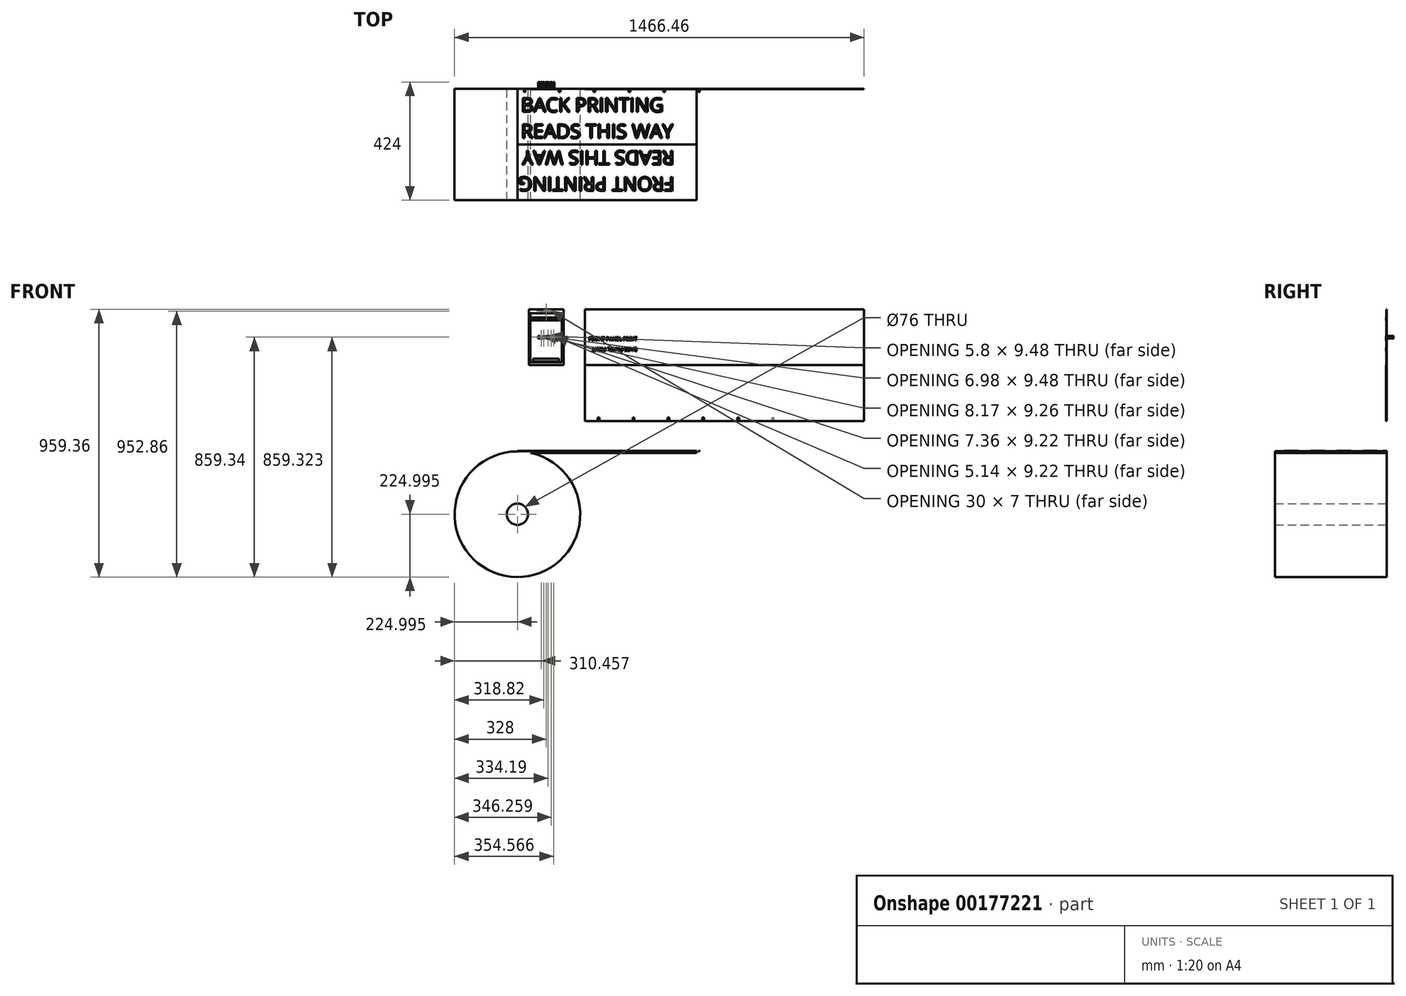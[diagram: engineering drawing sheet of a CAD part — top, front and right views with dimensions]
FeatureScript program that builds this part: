
annotation { "Feature Type Name" : "Feature", "Feature Type Description" : "" }
export const myFeature = defineFeature(function(context is Context, id is Id, definition is map)
    precondition{}
    {
        {
            assignVariable(context, id + "F0", {"name" : "hoogte", "anyValue" : 200});
        }
        {
            var Q0;
            Q0=qCreatedBy(makeId("Front.planeOp"),FACE);
            var sketch = newSketch(context, id + "F1", { "sketchPlane" : qUnion([Q0])});
            skLineSegment(sketch, "E0.bottom", {"start": v(-62.5, 100) * mm, "end": v(62.5, 100) * mm});
            skLineSegment(sketch, "E0.top", {"start": v(-62.5, -100) * mm, "end": v(62.5, -100) * mm});
            skLineSegment(sketch, "E0.left", {"start": v(-62.5, 100) * mm, "end": v(-62.5, -100) * mm});
            skLineSegment(sketch, "E0.right", {"start": v(62.5, 100) * mm, "end": v(62.5, -100) * mm});
            skLineSegment(sketch, "E1", {"start": v(-62.5, 76.41) * mm, "end": v(-61.09, 75) * mm});
            skLineSegment(sketch, "E2", {"start": v(-61.09, 75) * mm, "end": v(-62.5, 73.59) * mm});
            skLineSegment(sketch, "E3", {"start": v(62.5, 76.41) * mm, "end": v(61.09, 75) * mm});
            skLineSegment(sketch, "E4", {"start": v(61.09, 75) * mm, "end": v(62.5, 73.59) * mm});
            skLineSegment(sketch, "E5.bottom", {"start": v(138.46, 100) * mm, "end": v(1138.46, 100) * mm});
            skLineSegment(sketch, "E5.top", {"start": v(138.46, -300) * mm, "end": v(1138.46, -300) * mm});
            skLineSegment(sketch, "E5.left", {"start": v(138.46, 100) * mm, "end": v(138.46, -300) * mm});
            skLineSegment(sketch, "E5.right", {"start": v(1138.46, 100) * mm, "end": v(1138.46, -300) * mm});
            skLineSegment(sketch, "E6", {"start": v(138.46, -100) * mm, "end": v(1138.46, -100) * mm});
            skLineSegment(sketch, "E7", {"start": v(-62.5, 100) * mm, "end": v(62.5, -100) * mm, "construction": true});
            skLineSegment(sketch, "E8", {"start": v(62.5, 100) * mm, "end": v(-62.5, -100) * mm, "construction": true});
            skPoint(sketch, "E9", {"position": v(0, 0) * mm});
            skSolve(sketch);
        }
        {
            var Q0;
            {var subQ3=sQuery(id+"F1.wireOp",EDGE,"E0.bottom");Q0=makeQuery(id+"F1.imprint","IMPRINT",FACE,{"disambiguationData":[TD([[makeQuery(id+"F1.imprint","IMPRINT",EDGE,{"derivedFrom":subQ3}),-1.0]])]});}
            var Q1;
            Q1=makeQuery(id+"F1.imprint","IMPRINT",FACE,{"disambiguationData":[TD([[makeQuery(id+"F1.imprint","IMPRINT",EDGE,{"derivedFrom":sQuery(id+"F1.wireOp",EDGE,"E5.bottom")}),-1.0]])]});
            var Q2;
            {var subQ0=sQuery(id+"F1.wireOp",EDGE,"E5.top");Q2=makeQuery(id+"F1.imprint","IMPRINT",FACE,{"disambiguationData":[TD([[makeQuery(id+"F1.imprint","IMPRINT",EDGE,{"derivedFrom":subQ0}),1.0]])]});}
            extrude(context, id + "F2", {"entities" : qUnion([Q0, Q1, Q2]), "depth" : 1 * mm});
        }
        {
            var Q0;
            Q0=makeQuery(id+"F2.opExtrude","CAP_FACE",FACE,{"disambiguationData":[OSD([sQuery(id+"F1.wireOp",EDGE,"E0.bottom"),sQuery(id+"F1.wireOp",EDGE,"E0.top"),sQuery(id+"F1.wireOp",EDGE,"E0.left"),sQuery(id+"F1.wireOp",EDGE,"E0.right"),sQuery(id+"F1.wireOp",EDGE,"E1"),sQuery(id+"F1.wireOp",EDGE,"E2"),sQuery(id+"F1.wireOp",EDGE,"E3"),sQuery(id+"F1.wireOp",EDGE,"E4")])],"isStart":false});
            var sketch = newSketch(context, id + "F3", { "sketchPlane" : qUnion([Q0])});
            skLineSegment(sketch, "E10.0.0", {"start": v(62.5, 100) * mm, "end": v(-62.5, 100) * mm});
            skLineSegment(sketch, "E10.0.1", {"start": v(-62.5, 100) * mm, "end": v(-62.5, 76.41) * mm});
            skLineSegment(sketch, "E10.0.2", {"start": v(-62.5, 76.41) * mm, "end": v(-61.09, 75) * mm});
            skLineSegment(sketch, "E10.0.3", {"start": v(-61.09, 75) * mm, "end": v(-62.5, 73.59) * mm});
            skLineSegment(sketch, "E10.0.4", {"start": v(-62.5, 73.59) * mm, "end": v(-62.5, -100) * mm});
            skLineSegment(sketch, "E10.0.5", {"start": v(-62.5, -100) * mm, "end": v(62.5, -100) * mm});
            skLineSegment(sketch, "E10.0.6", {"start": v(62.5, -100) * mm, "end": v(62.5, 73.59) * mm});
            skLineSegment(sketch, "E10.0.7", {"start": v(62.5, 73.59) * mm, "end": v(61.09, 75) * mm});
            skLineSegment(sketch, "E10.0.8", {"start": v(61.09, 75) * mm, "end": v(62.5, 76.41) * mm});
            skLineSegment(sketch, "E10.0.9", {"start": v(62.5, 76.41) * mm, "end": v(62.5, 100) * mm});
            skLineSegment(sketch, "E11.bottom", {"start": v(-56.5, 85) * mm, "end": v(56.5, 85) * mm});
            skLineSegment(sketch, "E11.top", {"start": v(-56.5, -90) * mm, "end": v(56.5, -90) * mm});
            skLineSegment(sketch, "E11.left", {"start": v(-56.5, 85) * mm, "end": v(-56.5, -90) * mm});
            skLineSegment(sketch, "E11.right", {"start": v(56.5, 85) * mm, "end": v(56.5, -90) * mm});
            skLineSegment(sketch, "E12.bottom", {"start": v(-62.5, 100) * mm, "end": v(-59.5, 100) * mm});
            skLineSegment(sketch, "E12.top", {"start": v(-62.5, 88) * mm, "end": v(-59.5, 88) * mm});
            skLineSegment(sketch, "E12.left", {"start": v(-62.5, 100) * mm, "end": v(-62.5, 88) * mm});
            skLineSegment(sketch, "E12.right", {"start": v(-59.5, 100) * mm, "end": v(-59.5, 88) * mm});
            skLineSegment(sketch, "E13.bottom", {"start": v(62.5, 100) * mm, "end": v(59.5, 100) * mm});
            skLineSegment(sketch, "E13.top", {"start": v(62.5, 88) * mm, "end": v(59.5, 88) * mm});
            skLineSegment(sketch, "E13.left", {"start": v(62.5, 100) * mm, "end": v(62.5, 88) * mm});
            skLineSegment(sketch, "E13.right", {"start": v(59.5, 100) * mm, "end": v(59.5, 88) * mm});
            skLineSegment(sketch, "E14.bottom", {"start": v(-46.5, -77) * mm, "end": v(46.5, -77) * mm});
            skLineSegment(sketch, "E14.top", {"start": v(-46.5, -87) * mm, "end": v(46.5, -87) * mm});
            skLineSegment(sketch, "E14.left", {"start": v(-46.5, -77) * mm, "end": v(-46.5, -87) * mm});
            skLineSegment(sketch, "E14.right", {"start": v(46.5, -77) * mm, "end": v(46.5, -87) * mm});
            skSolve(sketch);
        }
        {
            var Q0;
            Q0=makeQuery(id+"F3.imprint","IMPRINT",FACE,{"disambiguationData":[TD([[makeQuery(id+"F3.imprint","IMPRINT",EDGE,{"derivedFrom":sQuery(id+"F3.wireOp",EDGE,"E11.bottom")}),-1.0]])]});
            var Q1;
            Q1=makeQuery(id+"F3.imprint","IMPRINT",FACE,{"disambiguationData":[TD([[makeQuery(id+"F3.imprint","IMPRINT",EDGE,{"derivedFrom":sQuery(id+"F3.wireOp",EDGE,"E12.bottom")}),-1.0]])]});
            var Q2;
            Q2=makeQuery(id+"F3.imprint","IMPRINT",FACE,{"disambiguationData":[TD([[makeQuery(id+"F3.imprint","IMPRINT",EDGE,{"derivedFrom":sQuery(id+"F3.wireOp",EDGE,"E13.bottom")}),-1.0]])]});
            extrude(context, id + "F4", {"entities" : qUnion([Q0, Q1, Q2]), "operationType" : NewBodyOperationType.REMOVE, "oppositeDirection" : true, "depth" : 0.5 * mm});
        }
        {
            var Q0;
            Q0=makeQuery(id+"F2.opExtrude","CAP_FACE",FACE,{"disambiguationData":[OSD([sQuery(id+"F1.wireOp",EDGE,"E5.bottom"),sQuery(id+"F1.wireOp",EDGE,"E5.left"),sQuery(id+"F1.wireOp",EDGE,"E5.right"),sQuery(id+"F1.wireOp",EDGE,"E6")])],"isStart":false});
            var sketch = newSketch(context, id + "F5", { "sketchPlane" : qUnion([Q0])});
            skLineSegment(sketch, "E15.0.0", {"start": v(1138.46, 100) * mm, "end": v(138.46, 100) * mm});
            skLineSegment(sketch, "E15.0.1", {"start": v(138.46, 100) * mm, "end": v(138.46, 100) * mm});
            skLineSegment(sketch, "E15.0.2", {"start": v(138.46, 100) * mm, "end": v(1138.46, 100) * mm});
            skLineSegment(sketch, "E15.0.3", {"start": v(1138.46, 100) * mm, "end": v(1138.46, 100) * mm});
            skLineSegment(sketch, "E16.bottom", {"start": v(184.68, -300) * mm, "end": v(190.68, -300) * mm});
            skLineSegment(sketch, "E16.top", {"start": v(184.68, -288) * mm, "end": v(190.68, -288) * mm});
            skLineSegment(sketch, "E16.left", {"start": v(184.68, -300) * mm, "end": v(184.68, -288) * mm});
            skLineSegment(sketch, "E16.right", {"start": v(190.68, -300) * mm, "end": v(190.68, -288) * mm});
            skLineSegment(sketch, "E17.1.0.0", {"start": v(309.68, -288) * mm, "end": v(315.68, -288) * mm});
            skLineSegment(sketch, "E17.1.0.1", {"start": v(309.68, -300) * mm, "end": v(309.68, -288) * mm});
            skLineSegment(sketch, "E17.1.0.2", {"start": v(309.68, -300) * mm, "end": v(315.68, -300) * mm});
            skLineSegment(sketch, "E17.1.0.3", {"start": v(315.68, -300) * mm, "end": v(315.68, -288) * mm});
            skLineSegment(sketch, "E17.2.0.0", {"start": v(434.68, -288) * mm, "end": v(440.68, -288) * mm});
            skLineSegment(sketch, "E17.2.0.1", {"start": v(434.68, -300) * mm, "end": v(434.68, -288) * mm});
            skLineSegment(sketch, "E17.2.0.2", {"start": v(434.68, -300) * mm, "end": v(440.68, -300) * mm});
            skLineSegment(sketch, "E17.2.0.3", {"start": v(440.68, -300) * mm, "end": v(440.68, -288) * mm});
            skLineSegment(sketch, "E17.direction1", {"start": v(184.68, -300) * mm, "end": v(309.68, -300) * mm, "construction": true});
            skLineSegment(sketch, "E18.0.3.0", {"start": v(559.68, -288) * mm, "end": v(565.68, -288) * mm});
            skLineSegment(sketch, "E18.3.3.0", {"start": v(559.68, -300) * mm, "end": v(559.68, -288) * mm});
            skLineSegment(sketch, "E18.6.3.0", {"start": v(559.68, -300) * mm, "end": v(565.68, -300) * mm});
            skLineSegment(sketch, "E18.9.3.0", {"start": v(565.68, -300) * mm, "end": v(565.68, -288) * mm});
            skLineSegment(sketch, "E18.0.4.0", {"start": v(684.68, -288) * mm, "end": v(690.68, -288) * mm});
            skLineSegment(sketch, "E18.3.4.0", {"start": v(684.68, -300) * mm, "end": v(684.68, -288) * mm});
            skLineSegment(sketch, "E18.6.4.0", {"start": v(684.68, -300) * mm, "end": v(690.68, -300) * mm});
            skLineSegment(sketch, "E18.9.4.0", {"start": v(690.68, -300) * mm, "end": v(690.68, -288) * mm});
            skLineSegment(sketch, "E19.0.5.0", {"start": v(809.68, -288) * mm, "end": v(815.68, -288) * mm});
            skLineSegment(sketch, "E19.3.5.0", {"start": v(809.68, -300) * mm, "end": v(809.68, -288) * mm});
            skLineSegment(sketch, "E19.6.5.0", {"start": v(809.68, -300) * mm, "end": v(815.68, -300) * mm});
            skLineSegment(sketch, "E19.9.5.0", {"start": v(815.68, -300) * mm, "end": v(815.68, -288) * mm});
            skSolve(sketch);
        }
        {
            var Q0;
            Q0=makeQuery(id+"F5.imprint","IMPRINT",FACE,{"disambiguationData":[TD([[makeQuery(id+"F5.imprint","IMPRINT",EDGE,{"derivedFrom":sQuery(id+"F5.wireOp",EDGE,"JLQzprwf-iRJq-cmRX-vWmS-HmgRmsplr5sc.top")}),-1.0]])]});
            var Q1;
            Q1=makeQuery(id+"F5.imprint","IMPRINT",FACE,{"disambiguationData":[TD([[makeQuery(id+"F5.imprint","IMPRINT",EDGE,{"derivedFrom":sQuery(id+"F5.wireOp",EDGE,"E16.bottom")}),1.0]])]});
            var Q2;
            Q2=makeQuery(id+"F5.imprint","IMPRINT",FACE,{"disambiguationData":[TD([[makeQuery(id+"F5.imprint","IMPRINT",EDGE,{"derivedFrom":sQuery(id+"F5.wireOp",EDGE,"E17.1.0.0")}),-1.0]])]});
            var Q3;
            Q3=makeQuery(id+"F5.imprint","IMPRINT",FACE,{"disambiguationData":[TD([[makeQuery(id+"F5.imprint","IMPRINT",EDGE,{"derivedFrom":sQuery(id+"F5.wireOp",EDGE,"E17.2.0.0")}),-1.0]])]});
            var Q4;
            Q4=makeQuery(id+"F5.imprint","IMPRINT",FACE,{"disambiguationData":[TD([[makeQuery(id+"F5.imprint","IMPRINT",EDGE,{"derivedFrom":sQuery(id+"F5.wireOp",EDGE,"E18.0.3.0")}),-1.0]])]});
            var Q5;
            Q5=makeQuery(id+"F5.imprint","IMPRINT",FACE,{"disambiguationData":[TD([[makeQuery(id+"F5.imprint","IMPRINT",EDGE,{"derivedFrom":sQuery(id+"F5.wireOp",EDGE,"E18.0.4.0")}),-1.0]])]});
            var Q6;
            Q6=makeQuery(id+"F5.imprint","IMPRINT",FACE,{"disambiguationData":[TD([[makeQuery(id+"F5.imprint","IMPRINT",EDGE,{"derivedFrom":sQuery(id+"F5.wireOp",EDGE,"E19.0.5.0")}),-1.0]])]});
            extrude(context, id + "F6", {"entities" : qUnion([Q0, Q1, Q2, Q3, Q4, Q5, Q6]), "operationType" : NewBodyOperationType.REMOVE, "oppositeDirection" : true, "depth" : 0.5 * mm});
        }
        {
            var Q0;
            Q0=qCreatedBy(makeId("Front.planeOp"),FACE);
            var sketch = newSketch(context, id + "F7", { "sketchPlane" : qUnion([Q0])});
            skCircle(sketch, "E20", {"center": v(-103, -634.36) * mm, "radius": 225 * mm});
            skLineSegment(sketch, "E21.bottom", {"start": v(-103, -408.35) * mm, "end": v(538.87, -408.35) * mm});
            skLineSegment(sketch, "E21.top", {"start": v(-103, -414.51) * mm, "end": v(538.87, -414.51) * mm});
            skLineSegment(sketch, "E21.left", {"start": v(-103, -414.51) * mm, "end": v(-103, -408.35) * mm});
            skLineSegment(sketch, "E21.right", {"start": v(538.87, -414.51) * mm, "end": v(538.87, -408.35) * mm});
            skCircle(sketch, "E22", {"center": v(-103, -634.36) * mm, "radius": 38 * mm});
            skSolve(sketch);
        }
        {
            var Q0;
            Q0=qSketchRegion(id+"F7",true);
            extrude(context, id + "F8", {"entities" : qUnion([Q0]), "depth" : (((getVariable(context, 'hoogte')) * 2)) * mm});
        }
        {
            var Q0;
            {var subQ0=sQuery(id+"F1.wireOp",EDGE,"E4");var subQ1=sQuery(id+"F1.wireOp",EDGE,"E2");var subQ2=sQuery(id+"F1.wireOp",EDGE,"E1");var subQ3=sQuery(id+"F1.wireOp",EDGE,"E0.right");var subQ4=sQuery(id+"F1.wireOp",EDGE,"E0.top");var subQ5=sQuery(id+"F1.wireOp",EDGE,"E0.bottom");var subQ6=sQuery(id+"F1.wireOp",EDGE,"E3");var subQ7=sQuery(id+"F1.wireOp",EDGE,"E0.left");Q0=makeQuery(id+"F4.boolean.opBoolean","SPLIT",FACE,{"disambiguationData":[TD([makeQuery(id+"F2.opExtrude","SWEPT_FACE",FACE,{"disambiguationData":[OSD([subQ5])]})])],"derivedFrom":makeQuery(id+"F2.opExtrude","CAP_FACE",FACE,{"disambiguationData":[OSD([subQ5,subQ4,subQ7,subQ3,subQ2,subQ1,subQ6,subQ0])],"isStart":false})});}
            var sketch = newSketch(context, id + "F9", { "sketchPlane" : qUnion([Q0])});
            skText(sketch, "E23", { "text": "BACKSIDE", "fontName": "OpenSans-Regular.ttf"});
            const initialGuessF9  = {"E23": [-0.03, -0.00465, 1, 0, 0.0093]};
            skSetInitialGuess(sketch, initialGuessF9);
            skSolve(sketch);
        }
        {
            var Q0;
            Q0=qSketchRegion(id+"F9",true);
            extrude(context, id + "F10", {"entities" : qUnion([Q0]), "operationType" : NewBodyOperationType.ADD, "depth" : 1 * mm, "hasSecondDirection" : true, "secondDirectionOppositeDirection" : true, "secondDirectionDepth" : 25 * mm});
        }
        {
            var Q0;
            {var subQ0=sQuery(id+"F1.wireOp",EDGE,"E5.bottom");var subQ1=sQuery(id+"F1.wireOp",EDGE,"E5.left");var subQ2=sQuery(id+"F1.wireOp",EDGE,"E5.right");Q0=makeQuery(id+"F6.boolean.opBoolean","SPLIT",FACE,{"disambiguationData":[TD([makeQuery(id+"F2.opExtrude","SWEPT_FACE",FACE,{"disambiguationData":[OSD([subQ0])]})])],"derivedFrom":makeQuery(id+"F2.opExtrude","CAP_FACE",FACE,{"disambiguationData":[OSD([subQ0,sQuery(id+"F1.wireOp",EDGE,"E5.top"),subQ1,subQ2])],"isStart":false})});}
            var sketch = newSketch(context, id + "F11", { "sketchPlane" : qUnion([Q0])});
            skText(sketch, "E24", { "text": "FRONT PANEL PRINT", "fontName": "AllertaStencil-Regular.ttf"});
            skLineSegment(sketch, "E25.0.0", {"start": v(1138.46, -100) * mm, "end": v(138.46, -100) * mm});
            skLineSegment(sketch, "E25.0.1", {"start": v(138.46, -100) * mm, "end": v(138.46, -300) * mm});
            skLineSegment(sketch, "E25.0.2", {"start": v(138.46, -300) * mm, "end": v(184.68, -300) * mm});
            skLineSegment(sketch, "E25.0.3", {"start": v(184.68, -300) * mm, "end": v(184.68, -288) * mm});
            skLineSegment(sketch, "E25.0.4", {"start": v(184.68, -288) * mm, "end": v(190.68, -288) * mm});
            skLineSegment(sketch, "E25.0.5", {"start": v(190.68, -288) * mm, "end": v(190.68, -300) * mm});
            skLineSegment(sketch, "E25.0.6", {"start": v(190.68, -300) * mm, "end": v(309.68, -300) * mm});
            skLineSegment(sketch, "E25.0.7", {"start": v(309.68, -300) * mm, "end": v(309.68, -288) * mm});
            skLineSegment(sketch, "E25.0.8", {"start": v(309.68, -288) * mm, "end": v(315.68, -288) * mm});
            skLineSegment(sketch, "E25.0.9", {"start": v(315.68, -288) * mm, "end": v(315.68, -300) * mm});
            skLineSegment(sketch, "E25.0.10", {"start": v(315.68, -300) * mm, "end": v(434.68, -300) * mm});
            skLineSegment(sketch, "E25.0.11", {"start": v(434.68, -300) * mm, "end": v(434.68, -288) * mm});
            skLineSegment(sketch, "E25.0.12", {"start": v(434.68, -288) * mm, "end": v(440.68, -288) * mm});
            skLineSegment(sketch, "E25.0.13", {"start": v(440.68, -288) * mm, "end": v(440.68, -300) * mm});
            skLineSegment(sketch, "E25.0.14", {"start": v(440.68, -300) * mm, "end": v(559.68, -300) * mm});
            skLineSegment(sketch, "E25.0.15", {"start": v(559.68, -300) * mm, "end": v(559.68, -288) * mm});
            skLineSegment(sketch, "E25.0.16", {"start": v(559.68, -288) * mm, "end": v(565.68, -288) * mm});
            skLineSegment(sketch, "E25.0.17", {"start": v(565.68, -288) * mm, "end": v(565.68, -300) * mm});
            skLineSegment(sketch, "E25.0.18", {"start": v(565.68, -300) * mm, "end": v(684.68, -300) * mm});
            skLineSegment(sketch, "E25.0.19", {"start": v(684.68, -300) * mm, "end": v(684.68, -288) * mm});
            skLineSegment(sketch, "E25.0.20", {"start": v(684.68, -288) * mm, "end": v(690.68, -288) * mm});
            skLineSegment(sketch, "E25.0.21", {"start": v(690.68, -288) * mm, "end": v(690.68, -300) * mm});
            skLineSegment(sketch, "E25.0.22", {"start": v(690.68, -300) * mm, "end": v(1138.46, -300) * mm});
            skLineSegment(sketch, "E25.0.23", {"start": v(1138.46, -300) * mm, "end": v(1138.46, -100) * mm});
            skText(sketch, "E26", { "text": "BACK PANEL PRINT", "fontName": "AllertaStencil-Regular.ttf"});
            skLineSegment(sketch, "E27", {"start": v(1088.46, -200) * mm, "end": v(1088.46, -201.37) * mm});
            const initialGuessF11  = {"E24": [0.1529, -0.0125, 1, 0, 0.0125], "E26": [0.32596, -0.0375, -1, 0, 0.0125]};
            skSetInitialGuess(sketch, initialGuessF11);
            skSolve(sketch);
        }
        {
            var Q0;
            Q0=qSketchRegion(id+"F11",true);
            extrude(context, id + "F12", {"entities" : qUnion([Q0]), "operationType" : NewBodyOperationType.ADD, "depth" : 1 * mm});
        }
        {
            var Q0;
            Q0=makeQuery(id+"F8.opExtrude","SWEPT_FACE",FACE,{"disambiguationData":[OSD([sQuery(id+"F7.wireOp",EDGE,"E21.bottom")])]});
            var sketch = newSketch(context, id + "F13", { "sketchPlane" : qUnion([Q0])});
            skText(sketch, "E28", { "text": "BACK PRINTING \nREADS THIS WAY", "fontName": "OpenSans-Regular.ttf"});
            skText(sketch, "E29", { "text": "FRONT PRINTING\nREADS THIS WAY", "fontName": "OpenSans-Regular.ttf"});
            skLineSegment(sketch, "E30", {"start": v(458.87, -304.1) * mm, "end": v(458.87, -366.67) * mm});
            skLineSegment(sketch, "E31", {"start": v(538.87, -200) * mm, "end": v(-103, -200) * mm, "construction": true});
            skLineSegment(sketch, "E32.bottom", {"start": v(538.87, -200) * mm, "end": v(-103, -200) * mm});
            skLineSegment(sketch, "E32.top", {"start": v(538.87, -199.95) * mm, "end": v(-103, -199.95) * mm});
            skLineSegment(sketch, "E32.left", {"start": v(538.87, -200) * mm, "end": v(538.87, -199.95) * mm});
            skLineSegment(sketch, "E32.right", {"start": v(-103, -200) * mm, "end": v(-103, -199.95) * mm});
            skLineSegment(sketch, "E33.bottom", {"start": v(538.87, -200.05) * mm, "end": v(-103, -200.05) * mm});
            skLineSegment(sketch, "E33.left", {"start": v(538.87, -200.05) * mm, "end": v(538.87, -200) * mm});
            skLineSegment(sketch, "E33.right", {"start": v(-103, -200.05) * mm, "end": v(-103, -200) * mm});
            skLineSegment(sketch, "E34.bottom", {"start": v(-80.23, 0) * mm, "end": v(-74.23, 0) * mm});
            skLineSegment(sketch, "E34.top", {"start": v(-80.23, -12) * mm, "end": v(-74.23, -12) * mm});
            skLineSegment(sketch, "E34.left", {"start": v(-80.23, 0) * mm, "end": v(-80.23, -12) * mm});
            skLineSegment(sketch, "E34.right", {"start": v(-74.23, 0) * mm, "end": v(-74.23, -12) * mm});
            skLineSegment(sketch, "E35.1.0.0", {"start": v(44.77, 0) * mm, "end": v(50.77, 0) * mm});
            skLineSegment(sketch, "E35.1.0.1", {"start": v(44.77, -12) * mm, "end": v(50.77, -12) * mm});
            skLineSegment(sketch, "E35.1.0.2", {"start": v(44.77, 0) * mm, "end": v(44.77, -12) * mm});
            skLineSegment(sketch, "E35.1.0.3", {"start": v(50.77, 0) * mm, "end": v(50.77, -12) * mm});
            skLineSegment(sketch, "E35.2.0.0", {"start": v(169.77, 0) * mm, "end": v(175.77, 0) * mm});
            skLineSegment(sketch, "E35.2.0.1", {"start": v(169.77, -12) * mm, "end": v(175.77, -12) * mm});
            skLineSegment(sketch, "E35.2.0.2", {"start": v(169.77, 0) * mm, "end": v(169.77, -12) * mm});
            skLineSegment(sketch, "E35.2.0.3", {"start": v(175.77, 0) * mm, "end": v(175.77, -12) * mm});
            skLineSegment(sketch, "E35.direction1", {"start": v(-80.23, -12) * mm, "end": v(44.77, -12) * mm, "construction": true});
            skLineSegment(sketch, "E36.0.3.0", {"start": v(294.77, 0) * mm, "end": v(300.77, 0) * mm});
            skLineSegment(sketch, "E36.3.3.0", {"start": v(294.77, -12) * mm, "end": v(300.77, -12) * mm});
            skLineSegment(sketch, "E36.6.3.0", {"start": v(294.77, 0) * mm, "end": v(294.77, -12) * mm});
            skLineSegment(sketch, "E36.9.3.0", {"start": v(300.77, 0) * mm, "end": v(300.77, -12) * mm});
            skLineSegment(sketch, "E36.0.4.0", {"start": v(419.77, 0) * mm, "end": v(425.77, 0) * mm});
            skLineSegment(sketch, "E36.3.4.0", {"start": v(419.77, -12) * mm, "end": v(425.77, -12) * mm});
            skLineSegment(sketch, "E36.6.4.0", {"start": v(419.77, 0) * mm, "end": v(419.77, -12) * mm});
            skLineSegment(sketch, "E36.9.4.0", {"start": v(425.77, 0) * mm, "end": v(425.77, -12) * mm});
            skLineSegment(sketch, "E36.0.5.0", {"start": v(544.77, 0) * mm, "end": v(550.77, 0) * mm});
            skLineSegment(sketch, "E36.3.5.0", {"start": v(544.77, -12) * mm, "end": v(550.77, -12) * mm});
            skLineSegment(sketch, "E36.6.5.0", {"start": v(544.77, 0) * mm, "end": v(544.77, -12) * mm});
            skLineSegment(sketch, "E36.9.5.0", {"start": v(550.77, 0) * mm, "end": v(550.77, -12) * mm});
            const initialGuessF13  = {"E28": [-0.09022, -0.08333, 1, 0, 0.05], "E29": [0.45887, -0.31667, -1, 0, 0.05]};
            skSetInitialGuess(sketch, initialGuessF13);
            skSolve(sketch);
        }
        {
            var Q0;
            Q0=qSketchRegion(id+"F13",true);
            extrude(context, id + "F14", {"entities" : qUnion([Q0]), "operationType" : NewBodyOperationType.ADD, "depth" : 1 * mm});
        }
        {
            var Q0;
            {var subQ0=sQuery(id+"F1.wireOp",EDGE,"E4");var subQ1=sQuery(id+"F1.wireOp",EDGE,"E2");var subQ2=sQuery(id+"F1.wireOp",EDGE,"E1");var subQ3=sQuery(id+"F1.wireOp",EDGE,"E0.right");var subQ4=sQuery(id+"F1.wireOp",EDGE,"E0.top");var subQ5=sQuery(id+"F1.wireOp",EDGE,"E0.bottom");var subQ6=sQuery(id+"F1.wireOp",EDGE,"E3");var subQ7=sQuery(id+"F1.wireOp",EDGE,"E0.left");Q0=makeQuery(id+"F4.boolean.opBoolean","SPLIT",FACE,{"disambiguationData":[TD([makeQuery(id+"F2.opExtrude","SWEPT_FACE",FACE,{"disambiguationData":[OSD([subQ5])]})])],"derivedFrom":makeQuery(id+"F2.opExtrude","CAP_FACE",FACE,{"disambiguationData":[OSD([subQ5,subQ4,subQ7,subQ3,subQ2,subQ1,subQ6,subQ0])],"isStart":false})});}
            var sketch = newSketch(context, id + "F15", { "sketchPlane" : qUnion([Q0])});
            skLineSegment(sketch, "E37.0.0", {"start": v(-59.5, 88) * mm, "end": v(-62.5, 88) * mm});
            skLineSegment(sketch, "E37.0.1", {"start": v(-62.5, 88) * mm, "end": v(-62.5, 76.41) * mm});
            skLineSegment(sketch, "E37.0.2", {"start": v(-62.5, 76.41) * mm, "end": v(-61.09, 75) * mm});
            skLineSegment(sketch, "E37.0.3", {"start": v(-61.09, 75) * mm, "end": v(-62.5, 73.59) * mm});
            skLineSegment(sketch, "E37.0.4", {"start": v(-62.5, 73.59) * mm, "end": v(-62.5, -100) * mm});
            skLineSegment(sketch, "E37.0.5", {"start": v(-62.5, -100) * mm, "end": v(62.5, -100) * mm});
            skLineSegment(sketch, "E37.0.6", {"start": v(62.5, -100) * mm, "end": v(62.5, 73.59) * mm});
            skLineSegment(sketch, "E37.0.7", {"start": v(62.5, 73.59) * mm, "end": v(61.09, 75) * mm});
            skLineSegment(sketch, "E37.0.8", {"start": v(61.09, 75) * mm, "end": v(62.5, 76.41) * mm});
            skLineSegment(sketch, "E37.0.9", {"start": v(62.5, 76.41) * mm, "end": v(62.5, 88) * mm});
            skLineSegment(sketch, "E37.0.10", {"start": v(62.5, 88) * mm, "end": v(59.5, 88) * mm});
            skLineSegment(sketch, "E37.0.11", {"start": v(59.5, 88) * mm, "end": v(59.5, 100) * mm});
            skLineSegment(sketch, "E37.0.12", {"start": v(59.5, 100) * mm, "end": v(-59.5, 100) * mm});
            skLineSegment(sketch, "E37.0.13", {"start": v(-59.5, 100) * mm, "end": v(-59.5, 88) * mm});
            skLineSegment(sketch, "E38.bottom", {"start": v(-13, 94) * mm, "end": v(13, 94) * mm});
            skLineSegment(sketch, "E38.top", {"start": v(-13, 90) * mm, "end": v(13, 90) * mm});
            skLineSegment(sketch, "E38.left", {"start": v(-13, 94) * mm, "end": v(-13, 90) * mm});
            skLineSegment(sketch, "E38.right", {"start": v(13, 94) * mm, "end": v(13, 90) * mm});
            skCircle(sketch, "E39", {"center": v(-13, 92) * mm, "radius": 2 * mm});
            skCircle(sketch, "E40", {"center": v(13, 92) * mm, "radius": 2 * mm});
            skCircle(sketch, "E41", {"center": v(0, 94) * mm, "radius": 3 * mm});
            skLineSegment(sketch, "E42", {"start": v(0, 100) * mm, "end": v(0, 85) * mm, "construction": true});
            skSolve(sketch);
        }
        {
            var Q0;
            {var subQ0=sQuery(id+"F15.wireOp",EDGE,"E41");var subQ1=sQuery(id+"F15.wireOp",EDGE,"E38.bottom");var subQ2=makeQuery(id+"F15.imprint","INTERSECT",VERTEX,{"disambiguationData":[OD(0.0)],"derivedFrom":[subQ1,subQ0]});Q0=makeQuery(id+"F15.imprint","IMPRINT",FACE,{"disambiguationData":[TD([[makeQuery(id+"F15.imprint","IMPRINT",EDGE,{"disambiguationData":[TD([[subQ2,-1.0]])],"derivedFrom":subQ1}),-1.0]])]});}
            var Q1;
            {var subQ0=sQuery(id+"F15.wireOp",EDGE,"E41");var subQ1=sQuery(id+"F15.wireOp",EDGE,"E38.bottom");var subQ2=makeQuery(id+"F15.imprint","INTERSECT",VERTEX,{"disambiguationData":[OD(0.0)],"derivedFrom":[subQ1,subQ0]});Q1=makeQuery(id+"F15.imprint","IMPRINT",FACE,{"disambiguationData":[TD([[makeQuery(id+"F15.imprint","IMPRINT",EDGE,{"disambiguationData":[TD([[subQ2,-1.0]])],"derivedFrom":subQ1}),1.0]])]});}
            var Q2;
            {var subQ4=sQuery(id+"F15.wireOp",EDGE,"E38.top");Q2=makeQuery(id+"F15.imprint","IMPRINT",FACE,{"disambiguationData":[TD([[makeQuery(id+"F15.imprint","IMPRINT",EDGE,{"derivedFrom":subQ4}),1.0]])]});}
            var Q3;
            {var subQ0=sQuery(id+"F15.wireOp",EDGE,"E38.left");Q3=makeQuery(id+"F15.imprint","IMPRINT",FACE,{"disambiguationData":[TD([[makeQuery(id+"F15.imprint","IMPRINT",EDGE,{"derivedFrom":subQ0}),1.0]])]});}
            var Q4;
            {var subQ0=sQuery(id+"F15.wireOp",EDGE,"E38.left");Q4=makeQuery(id+"F15.imprint","IMPRINT",FACE,{"disambiguationData":[TD([[makeQuery(id+"F15.imprint","IMPRINT",EDGE,{"derivedFrom":subQ0}),-1.0]])]});}
            var Q5;
            {var subQ0=sQuery(id+"F15.wireOp",EDGE,"E38.right");Q5=makeQuery(id+"F15.imprint","IMPRINT",FACE,{"disambiguationData":[TD([[makeQuery(id+"F15.imprint","IMPRINT",EDGE,{"derivedFrom":subQ0}),-1.0]])]});}
            var Q6;
            {var subQ0=sQuery(id+"F15.wireOp",EDGE,"E38.right");Q6=makeQuery(id+"F15.imprint","IMPRINT",FACE,{"disambiguationData":[TD([[makeQuery(id+"F15.imprint","IMPRINT",EDGE,{"derivedFrom":subQ0}),1.0]])]});}
            extrude(context, id + "F16", {"entities" : qUnion([Q0, Q1, Q2, Q3, Q4, Q5, Q6]), "operationType" : NewBodyOperationType.REMOVE, "oppositeDirection" : true, "depth" : 25 * mm});
        }
        {
            var Q0;
            {var subQ0=sQuery(id+"F1.wireOp",EDGE,"E4");var subQ1=sQuery(id+"F1.wireOp",EDGE,"E2");var subQ2=sQuery(id+"F1.wireOp",EDGE,"E1");var subQ3=sQuery(id+"F1.wireOp",EDGE,"E0.right");var subQ4=sQuery(id+"F1.wireOp",EDGE,"E0.top");var subQ5=sQuery(id+"F1.wireOp",EDGE,"E0.bottom");var subQ6=sQuery(id+"F1.wireOp",EDGE,"E3");var subQ7=sQuery(id+"F1.wireOp",EDGE,"E0.left");Q0=makeQuery(id+"F4.boolean.opBoolean","SPLIT",FACE,{"disambiguationData":[TD([makeQuery(id+"F2.opExtrude","SWEPT_FACE",FACE,{"disambiguationData":[OSD([subQ5])]})])],"derivedFrom":makeQuery(id+"F2.opExtrude","CAP_FACE",FACE,{"disambiguationData":[OSD([subQ5,subQ4,subQ7,subQ3,subQ2,subQ1,subQ6,subQ0])],"isStart":false})});}
            var sketch = newSketch(context, id + "F17", { "sketchPlane" : qUnion([Q0])});
            skLineSegment(sketch, "E43.0.0", {"start": v(-59.5, 88) * mm, "end": v(-62.5, 88) * mm});
            skLineSegment(sketch, "E43.0.1", {"start": v(-62.5, 88) * mm, "end": v(-62.5, 76.41) * mm});
            skLineSegment(sketch, "E43.0.2", {"start": v(-62.5, 76.41) * mm, "end": v(-61.09, 75) * mm});
            skLineSegment(sketch, "E43.0.3", {"start": v(-61.09, 75) * mm, "end": v(-62.5, 73.59) * mm});
            skLineSegment(sketch, "E43.0.4", {"start": v(-62.5, 73.59) * mm, "end": v(-62.5, -100) * mm});
            skLineSegment(sketch, "E43.0.5", {"start": v(-62.5, -100) * mm, "end": v(62.5, -100) * mm});
            skLineSegment(sketch, "E43.0.6", {"start": v(62.5, -100) * mm, "end": v(62.5, 73.59) * mm});
            skLineSegment(sketch, "E43.0.7", {"start": v(62.5, 73.59) * mm, "end": v(61.09, 75) * mm});
            skLineSegment(sketch, "E43.0.8", {"start": v(61.09, 75) * mm, "end": v(62.5, 76.41) * mm});
            skLineSegment(sketch, "E43.0.9", {"start": v(62.5, 76.41) * mm, "end": v(62.5, 88) * mm});
            skLineSegment(sketch, "E43.0.10", {"start": v(62.5, 88) * mm, "end": v(59.5, 88) * mm});
            skLineSegment(sketch, "E43.0.11", {"start": v(59.5, 88) * mm, "end": v(59.5, 100) * mm});
            skLineSegment(sketch, "E43.0.12", {"start": v(59.5, 100) * mm, "end": v(-59.5, 100) * mm});
            skLineSegment(sketch, "E43.0.13", {"start": v(-59.5, 100) * mm, "end": v(-59.5, 88) * mm});
            skLineSegment(sketch, "E44.0.0", {"start": v(56.5, 85) * mm, "end": v(-56.5, 85) * mm});
            skLineSegment(sketch, "E44.0.1", {"start": v(-56.5, 85) * mm, "end": v(-56.5, -90) * mm});
            skLineSegment(sketch, "E44.0.2", {"start": v(-56.5, -90) * mm, "end": v(56.5, -90) * mm});
            skLineSegment(sketch, "E44.0.3", {"start": v(56.5, -90) * mm, "end": v(56.5, 85) * mm});
            skLineSegment(sketch, "E45.bottom", {"start": v(-62.5, 70) * mm, "end": v(62.5, 70) * mm});
            skLineSegment(sketch, "E45.top", {"start": v(-62.5, 66) * mm, "end": v(62.5, 66) * mm});
            skLineSegment(sketch, "E45.left", {"start": v(-62.5, 70) * mm, "end": v(-62.5, 66) * mm});
            skLineSegment(sketch, "E45.right", {"start": v(62.5, 70) * mm, "end": v(62.5, 66) * mm});
            skLineSegment(sketch, "E46.bottom", {"start": v(-62.5, 64) * mm, "end": v(62.5, 64) * mm});
            skLineSegment(sketch, "E46.top", {"start": v(-62.5, 60) * mm, "end": v(62.5, 60) * mm});
            skLineSegment(sketch, "E46.left", {"start": v(-62.5, 64) * mm, "end": v(-62.5, 60) * mm});
            skLineSegment(sketch, "E46.right", {"start": v(62.5, 64) * mm, "end": v(62.5, 60) * mm});
            skLineSegment(sketch, "E47", {"start": v(-62.5, 66) * mm, "end": v(-62.5, 64) * mm, "construction": true});
            skLineSegment(sketch, "E48", {"start": v(-62.5, 65) * mm, "end": v(62.5, 65) * mm, "construction": true});
            skSolve(sketch);
        }
        {
            var Q0;
            {var subQ5=sQuery(id+"F17.wireOp",EDGE,"E45.left");Q0=makeQuery(id+"F17.imprint","IMPRINT",FACE,{"disambiguationData":[TD([[makeQuery(id+"F17.imprint","IMPRINT",EDGE,{"derivedFrom":subQ5}),1.0]])]});}
            var Q1;
            {var subQ0=sQuery(id+"F17.wireOp",EDGE,"E45.bottom");var subQ1=sQuery(id+"F17.wireOp",EDGE,"E44.0.1");var subQ2=makeQuery(id+"F17.imprint","INTERSECT",VERTEX,{"derivedFrom":[subQ1,subQ0]});Q1=makeQuery(id+"F17.imprint","IMPRINT",FACE,{"disambiguationData":[TD([[makeQuery(id+"F17.imprint","IMPRINT",EDGE,{"disambiguationData":[TD([[subQ2,-1.0]])],"derivedFrom":subQ1}),1.0]])]});}
            var Q2;
            {var subQ5=sQuery(id+"F17.wireOp",EDGE,"E45.right");Q2=makeQuery(id+"F17.imprint","IMPRINT",FACE,{"disambiguationData":[TD([[makeQuery(id+"F17.imprint","IMPRINT",EDGE,{"derivedFrom":subQ5}),-1.0]])]});}
            var Q3;
            {var subQ5=sQuery(id+"F17.wireOp",EDGE,"E46.right");Q3=makeQuery(id+"F17.imprint","IMPRINT",FACE,{"disambiguationData":[TD([[makeQuery(id+"F17.imprint","IMPRINT",EDGE,{"derivedFrom":subQ5}),-1.0]])]});}
            var Q4;
            {var subQ0=sQuery(id+"F17.wireOp",EDGE,"E46.bottom");var subQ1=sQuery(id+"F17.wireOp",EDGE,"E44.0.1");var subQ2=makeQuery(id+"F17.imprint","INTERSECT",VERTEX,{"derivedFrom":[subQ1,subQ0]});Q4=makeQuery(id+"F17.imprint","IMPRINT",FACE,{"disambiguationData":[TD([[makeQuery(id+"F17.imprint","IMPRINT",EDGE,{"disambiguationData":[TD([[subQ2,-1.0]])],"derivedFrom":subQ1}),1.0]])]});}
            var Q5;
            {var subQ5=sQuery(id+"F17.wireOp",EDGE,"E46.left");Q5=makeQuery(id+"F17.imprint","IMPRINT",FACE,{"disambiguationData":[TD([[makeQuery(id+"F17.imprint","IMPRINT",EDGE,{"derivedFrom":subQ5}),1.0]])]});}
            extrude(context, id + "F18", {"entities" : qUnion([Q0, Q1, Q2, Q3, Q4, Q5]), "operationType" : NewBodyOperationType.ADD, "depth" : 1 * mm});
        }
    });
